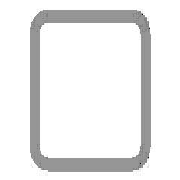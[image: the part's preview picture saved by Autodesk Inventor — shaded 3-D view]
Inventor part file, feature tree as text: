
AUTODESK INVENTOR PART (.ipt)
format: ipt  version: 2024 (Build 280153000, 153)  size: 149,504 bytes
history: native  units: mm (DEFAULTED — no unit token found)
features: other x4, extrude x2, sketch x2, plane x1
ambient origin geometry x8: Origin, YZ Plane, XZ Plane, XY Plane, X Axis, Y Axis, Z Axis, Center Point
bodies: Solid1 (feature_tree)
feature tree (9):
  parser-record x1  (decoder bookkeeping rows leaked as tree rows — omitted from the tree; the rows remain in map.json)
  other  "Driven Length"
  other  "Plano inicial"
  other  "Plano final"
  extrude  "Cuerpo"  TaperAngle=0.0deg  [1 undecoded]
  extrude  "Extrusión2"  Depth=50.8mm
  sketch  "Sketch3"  dims[d3=2190.0mm d4=0.0mm]
  plane  "Work Plane3"
  sketch  "Boceto5"  dims[d10=50.8mm d11=50.8mm d12=3.175mm d13=-0.0mm d14=2190.0mm d15=25.4mm d16=25.4mm d17=6.35mm d18=90.0deg d19=2190.0mm d20=18.034mm d21=18.034mm d22=18.034mm d23=1651.0mm d24=863.6mm d25=95.1484mm d26=15.875mm d27=0.0mm]
note: 1 required parameter value undecoded (feature->parameter linkage not recoverable at this tier; creation-order binding heuristic only, values carry confidence <= 0.55)
